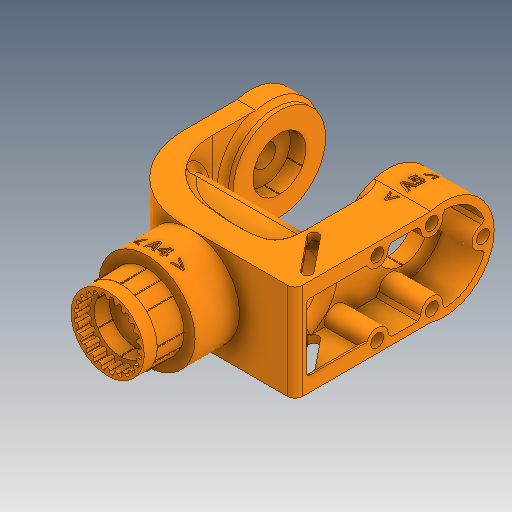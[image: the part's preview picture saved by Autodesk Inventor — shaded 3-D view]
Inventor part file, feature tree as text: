
AUTODESK INVENTOR PART (.ipt)
format: ipt  version: 2020 (Build 240168000, 168)  size: 2,372,096 bytes
history: native  units: in
note: dims shown in document units (in); Inventor stores cm internally (conversion verified against a paired STEP export)
features: sketch x49, extrude x44, projected_geometry x39, fillet x9, chamfer x8, plane x8, emboss x3
ambient origin geometry x8: Origin, YZ Plane, XZ Plane, XY Plane, X Axis, Y Axis, Z Axis, Center Point
bodies: Solid1 (feature_tree)
feature tree (160):
  extrude  "Extrusion1"  Depth=2.0472in
  extrude  "Extrusion2"  Depth=1.1063in
  chamfer  "Chamfer2"  Distance=0.5591in
  extrude  "Extrusion4"  Depth=0.0157in
  extrude  "Extrusion7"  Depth=0.2756in TaperAngle=0.0deg
  chamfer  "Chamfer4"  Distance=0.0394in
  extrude  "Extrusion8"  Depth=0.0157in
  sketch  "Sketch12"  dims[d39=1.4567in d57=0.0394in d58=0.0in]
  plane  "Work Plane1"
  sketch  "Sketch13"  dims[d59=0.315in d60=0.125in d61=0.0137in d67=0.0157in]
  extrude  "Extrusion10"  Depth=0.0394in TaperAngle=0.0deg
  extrude  "Extrusion11"  Depth=0.0866in
  chamfer  "Chamfer5"  Distance=9.4488in Angle=360.0deg
  extrude  "Extrusion12"  Depth=0.2756in TaperAngle=0.0deg
  plane  "Work Plane2"
  extrude  "Extrusion13"  Depth=0.315in
  plane  "Work Plane3"
  extrude  "Extrusion14"  Depth=1.0236in
  extrude  "Extrusion15"  Depth=0.8858in
  extrude  "Extrusion16"  Depth=0.3937in
  extrude  "Extrusion17"  Depth=1.378in
  sketch  "Sketch21"  dims[d107=0.315in d108=0.0in d109=0.315in d110=0.125in d111=0.0137in]
  extrude  "Extrusion19"  Depth=0.5906in
  sketch  "Sketch23"  dims[d112=1.0in d113=0.0in d114=1.0236in]
  extrude  "Extrusion20"  Depth=0.1575in TaperAngle=0.0deg
  extrude  "Extrusion21"  Depth=0.1575in TaperAngle=0.0deg
  extrude  "Extrusion22"  Depth=4.2323in
  extrude  "Extrusion23"  Depth=0.1575in
  extrude  "Extrusion24"  Depth=1.1024in
  extrude  "Extrusion25"  Depth=0.4921in
  extrude  "Extrusion26"  Depth=0.75in
  extrude  "Extrusion27"  Depth=0.1575in TaperAngle=0.0deg
  extrude  "Extrusion28"  Depth=0.1575in
  extrude  "Extrusion29"  Depth=0.1575in
  plane  "Work Plane4"
  extrude  "Extrusion30"  Depth=0.3937in TaperAngle=0.0deg
  fillet  "Fillet1"  Radius=0.3937in
  fillet  "Fillet2"  Radius=0.315in
  extrude  "Extrusion31"  Depth=0.315in TaperAngle=0.0deg
  extrude  "Extrusion32"  Depth=0.315in TaperAngle=0.0deg
  extrude  "Extrusion33"  Depth=0.3937in TaperAngle=0.0deg
  fillet  "Fillet3"  Radius=0.2165in
  extrude  "Extrusion34"  Depth=0.4724in
  chamfer  "Chamfer6"  Distance=0.2756in
  chamfer  "Chamfer7"  Distance=0.0394in
  extrude  "Extrusion35"  Depth=0.0394in
  extrude  "Extrusion36"  Depth=0.1575in TaperAngle=0.0deg
  fillet  "Fillet5"  Radius=0.1575in
  extrude  "Extrusion38"  Depth=0.315in
  extrude  "Extrusion39"  Depth=0.0157in
  extrude  "Extrusion40"  Depth=1.0in TaperAngle=0.0deg
  extrude  "Extrusion41"  Depth=0.3937in
  chamfer  "Chamfer8"  Distance=0.3937in
  extrude  "Extrusion42"  Depth=0.0787in
  plane  "Work Plane6"
  emboss  "Emboss1"
  emboss  "Emboss2"
  plane  "Work Plane7"
  emboss  "Emboss3"
  extrude  "Extrusion43"  Depth=0.1181in
  fillet  "Fillet9"  Radius=1.0039in
  chamfer  "Chamfer10"  Distance=0.1181in
  extrude  "Extrusion44"  Depth=0.1181in
  extrude  "Extrusion45"  Depth=0.0394in
  fillet  "Fillet12"  Radius=0.2047in
  fillet  "Fillet13"  [1 undecoded]
  plane  "Work Plane8"
  extrude  "Extrusion46"  Depth=0.0787in
  plane  "Work Plane9"
  extrude  "Extrusion47"  Depth=0.0787in
  fillet  "Fillet14"  Radius=0.0787in
  extrude  "Extrusion48"  Depth=0.0787in
  extrude  "Extrusion49"  Depth=0.0394in
  fillet  "Fillet15"  Radius=0.2756in
  chamfer  "Chamfer13"  Distance=0.4724in
  extrude  "Extrusion50"  Depth=0.0394in
  sketch  "Sketch62"  dims[d235=0.0197in d236=0.1181in d237=0.1181in d238=0.2047in d239=0.2047in d240=0.0in d241=0.0in d243=0.0787in d244=0.0787in d251=0.0787in d252=0.0787in d253=0.2756in d254=0.4724in d255=0.2756in d256=0.4724in d257=0.2756in d258=0.4724in d259=0.2756in d260=0.4724in d261=0.1575in d262=0.0in d263=0.0787in d264=0.125in d265=45.0deg d266=1.0in d267=0.0in d269=0.0394in d270=0.0in d271=0.0394in d272=0.0in d273=0.0394in d274=0.0in d275=0.0039in d276=0.0787in d277=1.0in d278=0.0in d279=0.122in d282=0.1378in d283=0.2047in d288=0.0394in d289=0.125in d290=45.0deg d291=0.5709in d292=0.0in d293=0.2835in d294=0.0in d295=0.2361in d296=0.0315in d297=1.1811in d298=0.315in d299=0.0984in d300=0.0in d301=0.0984in d302=0.0984in d303=0.0in d304=0.0256in d305=0.1575in d306=0.0in d307=0.1575in d308=0.0in d315=0.1575in d317=0.1181in d318=0.0787in d319=45.0deg d320=0.1575in d321=0.1575in d322=0.0394in d323=0.0in]
  sketch  "Sketch1"  dims[d0=0.6299in d1=2.0472in]
  sketch  "Sketch2"  dims[d2=0.9449in d3=0.0in d4=1.1063in]
  sketch  "Sketch4"  dims[d5=1.5748in d6=0.5591in d7=0.0in]
  sketch  "Sketch8"  dims[d11=0.5591in d12=0.125in d13=0.0137in d25=0.0157in]
  projected_geometry  "Projected Loop2"
  sketch  "Sketch10"  dims[d26=6.2992in d28=360.0deg d30=0.2756in d31=0.0in]
  sketch  "Sketch14"  dims[d68=4.7244in d70=360.0deg d72=0.0394in d73=0.0in]
  sketch  "Sketch15"  dims[d83=0.0591in d84=0.0866in]
  projected_geometry  "Projected Loop4"
  sketch  "Sketch16"  dims[d85=0.0827in]
  sketch  "Sketch17"  dims[d86=0.0827in]
  projected_geometry  "Projected Loop5"
  sketch  "Sketch18"  dims[d87=0.0827in d88=9.4488in d90=360.0deg]
  projected_geometry  "Projected Loop6"
  projected_geometry  "Projected Loop7"
  sketch  "Sketch19"  dims[d92=0.2756in]
  projected_geometry  "Projected Loop8"
  projected_geometry  "Projected Loop9"
  sketch  "Sketch20"  dims[d94=9.4488in d95=0.0827in d96=0.0827in d97=0.0827in d98=360.0deg d105=0.2756in d106=0.0in]
  projected_geometry  "Projected Loop10"
  projected_geometry  "Projected Loop11"
  projected_geometry  "Projected Loop12"
  projected_geometry  "Projected Loop13"
  sketch  "Sketch25"  dims[d115=0.7874in d117=0.8858in]
  sketch  "Sketch26"  dims[d118=2.7559in d119=0.3937in]
  projected_geometry  "Projected Loop16"
  projected_geometry  "Projected Loop17"
  sketch  "Sketch27"  dims[d120=0.5906in d121=1.378in]
  projected_geometry  "Projected Loop18"
  projected_geometry  "Projected Loop19"
  sketch  "Sketch28"  dims[d123=3.4941in d124=0.5906in]
  projected_geometry  "Projected Loop20"
  projected_geometry  "Projected Loop21"
  sketch  "Sketch29"  dims[d126=1.9685in d129=0.1575in d130=0.0in]
  projected_geometry  "Projected Loop22"
  projected_geometry  "Projected Loop23"
  sketch  "Sketch30"  dims[d131=-2.0472in d132=0.1575in d133=0.0in]
  projected_geometry  "Projected Loop24"
  sketch  "Sketch31"  dims[d134=2.126in d136=4.2323in]
  sketch  "Sketch32"  dims[d137=0.1575in d138=0.1575in]
  sketch  "Sketch34"  dims[d139=0.4921in d140=0.0in d141=1.1024in]
  projected_geometry  "Projected Loop25"
  sketch  "Sketch35"  dims[d142=1.1614in d143=0.4921in]
  sketch  "Sketch36"  dims[d144=0.3445in d145=0.75in]
  projected_geometry  "Projected Loop26"
  sketch  "Sketch37"  dims[d146=0.1575in d147=0.0in d148=0.2165in d149=0.0in]
  projected_geometry  "Projected Loop27"
  sketch  "Sketch38"  dims[d152=1.0039in d153=0.0in d154=0.1575in]
  projected_geometry  "Projected Loop28"
  sketch  "Sketch39"  dims[d155=0.1575in d160=1.1811in]
  projected_geometry  "Projected Loop29"
  sketch  "Sketch40"  dims[d161=0.1969in d162=0.0in d163=0.315in d164=0.0in d165=0.3937in d166=0.0in d167=0.315in d168=0.0in]
  sketch  "Sketch41"  dims[d169=0.315in d170=0.0in d171=0.315in d172=0.0in]
  projected_geometry  "Projected Loop30"
  sketch  "Sketch43"  dims[d173=0.315in d174=0.0in d175=0.315in d176=0.0in]
  projected_geometry  "Projected Loop31"
  sketch  "Sketch44"  dims[d177=1.1024in d178=0.3937in d179=0.0in d180=0.2165in d181=0.0in]
  sketch  "Sketch45"  dims[d183=-0.0197in d184=0.4724in d185=0.2756in d186=0.0in]
  sketch  "Sketch46"  dims[d187=0.5512in]
  projected_geometry  "Projected Loop32"
  sketch  "Sketch47"  dims[d188=0.2165in d189=0.0394in d190=0.0in]
  projected_geometry  "Projected Loop33"
  sketch  "Sketch48"  dims[d191=0.0394in d192=0.0in d193=0.001in]
  sketch  "Sketch49"  dims[d194=0.001in d195=1.0in d196=0.0in d197=0.1575in]
  sketch  "Sketch50"  dims[d198=1.0in d199=0.0in d200=0.315in d201=0.125in d202=0.0137in]
  sketch  "Sketch52"  dims[d203=0.315in d204=0.125in d205=0.0137in d206=0.0157in]
  sketch  "Sketch53"  dims[d207=2.3622in d209=360.0deg d211=1.0in d212=0.0in]
  projected_geometry  "Projected Loop35"
  projected_geometry  "Projected Loop36"
  projected_geometry  "Projected Loop37"
  projected_geometry  "Projected Loop38"
  projected_geometry  "Projected Loop39"
  sketch  "Sketch54"  dims[d213=1.0in d214=0.0in d221=0.1969in d222=0.3937in d223=0.0in]
  projected_geometry  "Projected Loop40"
  sketch  "Sketch56"  dims[d224=0.1575in d225=0.0787in]
  sketch  "Sketch57"  dims[d226=0.1969in d227=0.0in d229=0.1181in d230=1.0039in]
  sketch  "Sketch59"  dims[d231=0.4134in]
  projected_geometry  "Projected Loop41"
  sketch  "Sketch60"  dims[d232=0.5118in]
  projected_geometry  "Projected Loop42"
  sketch  "Sketch61"  dims[d233=0.0984in]
  projected_geometry  "Projected Loop43"
  projected_geometry  "Projected Loop44"
note: 1 required parameter value undecoded (feature->parameter linkage not recoverable at this tier; creation-order binding heuristic only, values carry confidence <= 0.55)
